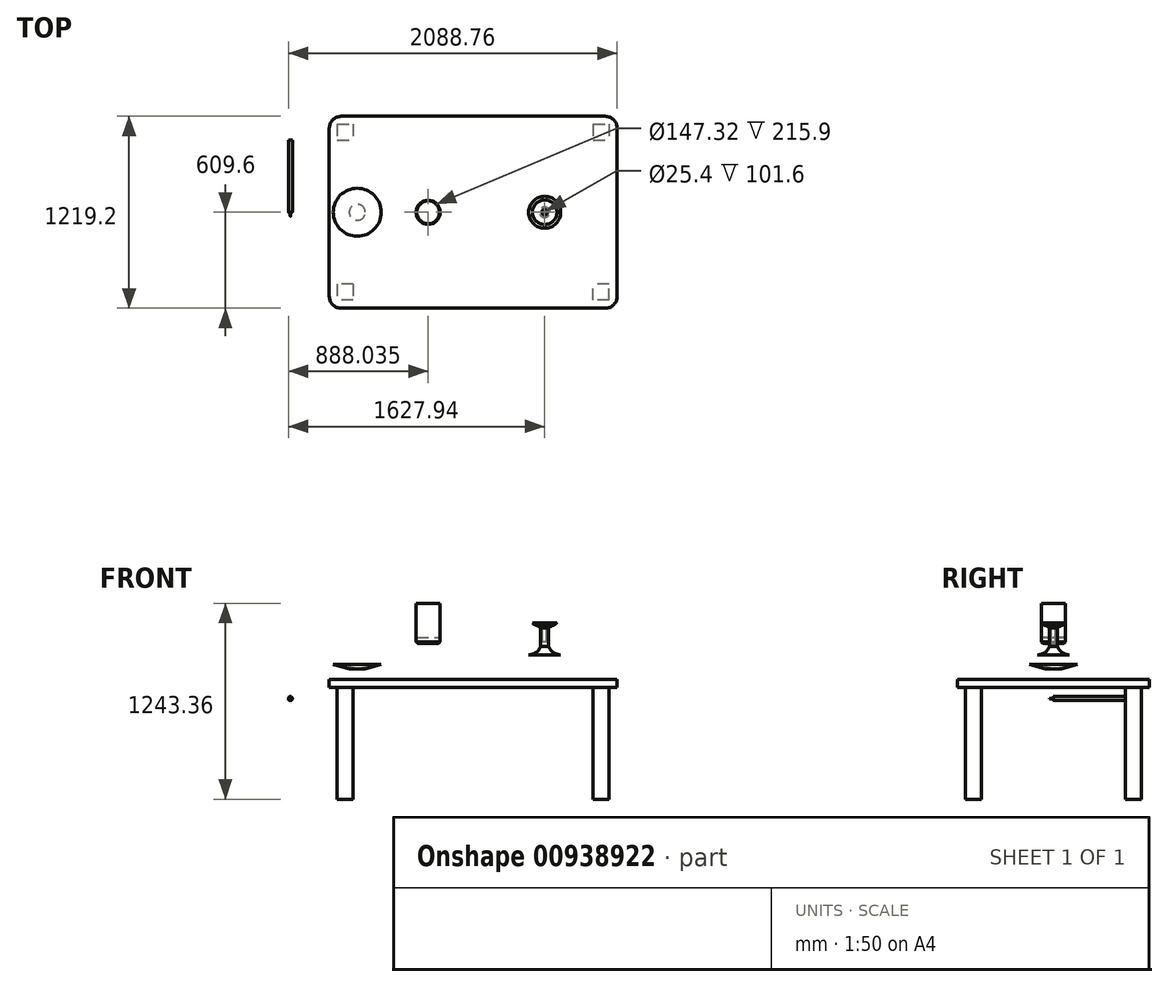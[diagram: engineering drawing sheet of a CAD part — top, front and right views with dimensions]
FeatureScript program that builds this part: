
annotation { "Feature Type Name" : "Feature", "Feature Type Description" : "" }
export const myFeature = defineFeature(function(context is Context, id is Id, definition is map)
    precondition{}
    {
        {
            var Q0;
            Q0=qCreatedBy(makeId("Top.planeOp"),FACE);
            var sketch = newSketch(context, id + "F0", { "sketchPlane" : qUnion([Q0])});
            skLineSegment(sketch, "E0.bottom", {"start": v(-838.2, 609.6) * mm, "end": v(838.2, 609.6) * mm});
            skLineSegment(sketch, "E0.top", {"start": v(-838.2, -609.6) * mm, "end": v(838.2, -609.6) * mm});
            skLineSegment(sketch, "E0.left", {"start": v(-914.4, 533.4) * mm, "end": v(-914.4, -533.4) * mm});
            skLineSegment(sketch, "E0.right", {"start": v(914.4, 533.4) * mm, "end": v(914.4, -533.4) * mm});
            skPoint(sketch, "E0.middle", {"position": v(0, 0) * mm});
            skLineSegment(sketch, "E1.bottom", {"start": v(-863.6, 558.8) * mm, "end": v(-762, 558.8) * mm});
            skLineSegment(sketch, "E1.top", {"start": v(-863.6, 457.2) * mm, "end": v(-762, 457.2) * mm});
            skLineSegment(sketch, "E1.left", {"start": v(-863.6, 558.8) * mm, "end": v(-863.6, 457.2) * mm});
            skLineSegment(sketch, "E1.right", {"start": v(-762, 558.8) * mm, "end": v(-762, 457.2) * mm});
            skLineSegment(sketch, "E2.bottom", {"start": v(762, 558.8) * mm, "end": v(863.6, 558.8) * mm});
            skLineSegment(sketch, "E2.top", {"start": v(762, 457.2) * mm, "end": v(863.6, 457.2) * mm});
            skLineSegment(sketch, "E2.left", {"start": v(762, 558.8) * mm, "end": v(762, 457.2) * mm});
            skLineSegment(sketch, "E2.right", {"start": v(863.6, 558.8) * mm, "end": v(863.6, 457.2) * mm});
            skLineSegment(sketch, "E3.bottom", {"start": v(863.6, -558.8) * mm, "end": v(762, -558.8) * mm});
            skLineSegment(sketch, "E3.top", {"start": v(863.6, -457.2) * mm, "end": v(762, -457.2) * mm});
            skLineSegment(sketch, "E3.left", {"start": v(863.6, -558.8) * mm, "end": v(863.6, -457.2) * mm});
            skLineSegment(sketch, "E3.right", {"start": v(762, -558.8) * mm, "end": v(762, -457.2) * mm});
            skLineSegment(sketch, "E4.bottom", {"start": v(-762, -457.2) * mm, "end": v(-863.6, -457.2) * mm});
            skLineSegment(sketch, "E4.top", {"start": v(-762, -558.8) * mm, "end": v(-863.6, -558.8) * mm});
            skLineSegment(sketch, "E4.left", {"start": v(-762, -457.2) * mm, "end": v(-762, -558.8) * mm});
            skLineSegment(sketch, "E4.right", {"start": v(-863.6, -457.2) * mm, "end": v(-863.6, -558.8) * mm});
            skPoint(sketch, "E5.visualSharp", {"position": v(-914.4, 609.6) * mm});
            skArc(sketch, "E5.filletArc", {"start": v(-838.2, 609.6) * mm, "mid": v(-892.08, 587.28) * mm, "end": v(-914.4, 533.4) * mm});
            skPoint(sketch, "E6.visualSharp", {"position": v(914.4, 609.6) * mm});
            skArc(sketch, "E6.filletArc", {"start": v(914.4, 533.4) * mm, "mid": v(892.08, 587.28) * mm, "end": v(838.2, 609.6) * mm});
            skPoint(sketch, "E7.visualSharp", {"position": v(914.4, -609.6) * mm});
            skArc(sketch, "E7.filletArc", {"start": v(838.2, -609.6) * mm, "mid": v(892.08, -587.28) * mm, "end": v(914.4, -533.4) * mm});
            skPoint(sketch, "E8.visualSharp", {"position": v(-914.4, -609.6) * mm});
            skArc(sketch, "E8.filletArc", {"start": v(-914.4, -533.4) * mm, "mid": v(-892.08, -587.28) * mm, "end": v(-838.2, -609.6) * mm});
            skSolve(sketch);
        }
        {
            var Q0;
            Q0=makeQuery(id+"F0.imprint","IMPRINT",FACE,{"disambiguationData":[TD([[makeQuery(id+"F0.imprint","IMPRINT",EDGE,{"derivedFrom":sQuery(id+"F0.wireOp",EDGE,"E0.bottom")}),-1.0]])]});
            var Q1;
            Q1=makeQuery(id+"F0.imprint","IMPRINT",FACE,{"disambiguationData":[TD([[makeQuery(id+"F0.imprint","IMPRINT",EDGE,{"derivedFrom":sQuery(id+"F0.wireOp",EDGE,"E4.bottom")}),1.0]])]});
            var Q2;
            Q2=makeQuery(id+"F0.imprint","IMPRINT",FACE,{"disambiguationData":[TD([[makeQuery(id+"F0.imprint","IMPRINT",EDGE,{"derivedFrom":sQuery(id+"F0.wireOp",EDGE,"E3.bottom")}),-1.0]])]});
            var Q3;
            Q3=makeQuery(id+"F0.imprint","IMPRINT",FACE,{"disambiguationData":[TD([[makeQuery(id+"F0.imprint","IMPRINT",EDGE,{"derivedFrom":sQuery(id+"F0.wireOp",EDGE,"E2.bottom")}),-1.0]])]});
            var Q4;
            Q4=makeQuery(id+"F0.imprint","IMPRINT",FACE,{"disambiguationData":[TD([[makeQuery(id+"F0.imprint","IMPRINT",EDGE,{"derivedFrom":sQuery(id+"F0.wireOp",EDGE,"E1.bottom")}),-1.0]])]});
            extrude(context, id + "F1", {"entities" : qUnion([Q0, Q1, Q2, Q3, Q4]), "depth" : 50.8 * mm, "offsetDistance" : 25.4 * mm});
        }
        {
            var Q0;
            Q0=makeQuery(id+"F0.imprint","IMPRINT",FACE,{"disambiguationData":[TD([[makeQuery(id+"F0.imprint","IMPRINT",EDGE,{"derivedFrom":sQuery(id+"F0.wireOp",EDGE,"E4.bottom")}),1.0]])]});
            var Q1;
            Q1=makeQuery(id+"F0.imprint","IMPRINT",FACE,{"disambiguationData":[TD([[makeQuery(id+"F0.imprint","IMPRINT",EDGE,{"derivedFrom":sQuery(id+"F0.wireOp",EDGE,"E1.bottom")}),-1.0]])]});
            var Q2;
            Q2=makeQuery(id+"F0.imprint","IMPRINT",FACE,{"disambiguationData":[TD([[makeQuery(id+"F0.imprint","IMPRINT",EDGE,{"derivedFrom":sQuery(id+"F0.wireOp",EDGE,"E2.bottom")}),-1.0]])]});
            var Q3;
            Q3=makeQuery(id+"F0.imprint","IMPRINT",FACE,{"disambiguationData":[TD([[makeQuery(id+"F0.imprint","IMPRINT",EDGE,{"derivedFrom":sQuery(id+"F0.wireOp",EDGE,"E3.bottom")}),-1.0]])]});
            extrude(context, id + "F2", {"entities" : qUnion([Q0, Q1, Q2, Q3]), "operationType" : NewBodyOperationType.ADD, "oppositeDirection" : true, "depth" : 711.2 * mm, "offsetDistance" : 25.4 * mm});
        }
        {
            var Q0;
            Q0=qCreatedBy(makeId("Front.planeOp"),FACE);
            var sketch = newSketch(context, id + "F3", { "sketchPlane" : qUnion([Q0])});
            skLineSegment(sketch, "E9", {"start": v(-286.32, 278.16) * mm, "end": v(-286.32, 532.16) * mm, "construction": true});
            skLineSegment(sketch, "E10.bottom", {"start": v(-286.32, 278.16) * mm, "end": v(-210.12, 278.16) * mm});
            skLineSegment(sketch, "E10.top", {"start": v(-286.32, 316.26) * mm, "end": v(-210.12, 316.26) * mm});
            skLineSegment(sketch, "E10.left", {"start": v(-286.32, 278.16) * mm, "end": v(-286.32, 316.26) * mm});
            skLineSegment(sketch, "E10.right", {"start": v(-210.12, 278.16) * mm, "end": v(-210.12, 316.26) * mm});
            skLineSegment(sketch, "E11.bottom", {"start": v(-210.12, 316.26) * mm, "end": v(-212.66, 316.26) * mm});
            skLineSegment(sketch, "E11.top", {"start": v(-210.12, 532.16) * mm, "end": v(-212.66, 532.16) * mm});
            skLineSegment(sketch, "E11.left", {"start": v(-210.12, 316.26) * mm, "end": v(-210.12, 532.16) * mm});
            skLineSegment(sketch, "E11.right", {"start": v(-212.66, 316.26) * mm, "end": v(-212.66, 532.16) * mm});
            skSolve(sketch);
        }
        {
            var Q0;
            Q0=makeQuery(id+"F3.imprint","IMPRINT",FACE,{"disambiguationData":[TD([[makeQuery(id+"F3.imprint","IMPRINT",EDGE,{"derivedFrom":sQuery(id+"F3.wireOp",EDGE,"E10.bottom")}),1.0]])]});
            var Q1;
            Q1=makeQuery(id+"F3.imprint","IMPRINT",FACE,{"disambiguationData":[TD([[makeQuery(id+"F3.imprint","IMPRINT",EDGE,{"derivedFrom":sQuery(id+"F3.wireOp",EDGE,"E11.top")}),1.0]])]});
            var Q2;
            Q2=sQuery(id+"F3.wireOp",EDGE,"E9");
            revolve(context, id + "F4", {"surfaceOperationType" : NewSurfaceOperationType.NEW, "entities" : qUnion([Q0, Q1]), "axis" : qUnion([Q2]), "revolveType" : RevolveType.FULL});
        }
        {
            var Q0;
            Q0=makeQuery(id+"F4.opRevolve","SWEPT_EDGE",EDGE,{"disambiguationData":[OSD([sQuery(id+"F3.wireOp",EDGE,"E10.bottom"),sQuery(id+"F3.wireOp",EDGE,"E10.right")])]});
            chamfer(context, id + "F5", {"entities" : qUnion([Q0]), "width" : 10.16 * mm, "tangentPropagation" : true});
        }
        {
            var Q0;
            Q0=qCreatedBy(makeId("Front.planeOp"),FACE);
            var sketch = newSketch(context, id + "F6", { "sketchPlane" : qUnion([Q0])});
            skLineSegment(sketch, "E12", {"start": v(-736.83, 117.03) * mm, "end": v(-736.83, 258.84) * mm});
            skLineSegment(sketch, "E13", {"start": v(-736.83, 117.03) * mm, "end": v(-787.63, 117.03) * mm});
            skLineSegment(sketch, "E14", {"start": v(-787.63, 117.03) * mm, "end": v(-889.23, 144.25) * mm});
            skLineSegment(sketch, "E15", {"start": v(-889.23, 144.25) * mm, "end": v(-736.83, 119.57) * mm});
            skSolve(sketch);
        }
        {
            var Q0;
            {var subQ0=sQuery(id+"F6.wireOp",EDGE,"E13");Q0=makeQuery(id+"F6.imprint","IMPRINT",FACE,{"disambiguationData":[TD([[makeQuery(id+"F6.imprint","IMPRINT",EDGE,{"derivedFrom":subQ0}),-1.0]])]});}
            var Q1;
            Q1=sQuery(id+"F6.wireOp",EDGE,"E12");
            revolve(context, id + "F7", {"surfaceOperationType" : NewSurfaceOperationType.NEW, "entities" : qUnion([Q0]), "axis" : qUnion([Q1]), "revolveType" : RevolveType.FULL});
        }
        {
            var Q0;
            Q0=qCreatedBy(makeId("Front.planeOp"),FACE);
            var sketch = newSketch(context, id + "F8", { "sketchPlane" : qUnion([Q0])});
            skCircle(sketch, "E16", {"center": v(-1161.66, -71.9) * mm, "radius": 12.7 * mm});
            skCircle(sketch, "E17", {"center": v(-1161.66, -71.9) * mm, "radius": 1.27 * mm});
            skSolve(sketch);
        }
        {
            var Q0;
            Q0=makeQuery(id+"F8.imprint","IMPRINT",FACE,{"disambiguationData":[TD([[makeQuery(id+"F8.imprint","IMPRINT",EDGE,{"derivedFrom":sQuery(id+"F8.wireOp",EDGE,"E16")}),1.0]])]});
            var Q1;
            Q1=makeQuery(id+"F8.imprint","IMPRINT",FACE,{"disambiguationData":[TD([[makeQuery(id+"F8.imprint","IMPRINT",EDGE,{"derivedFrom":sQuery(id+"F8.wireOp",EDGE,"E17")}),1.0]])]});
            extrude(context, id + "F9", {"entities" : qUnion([Q0, Q1]), "oppositeDirection" : true, "depth" : 457.2 * mm, "offsetDistance" : 25.4 * mm});
        }
        {
            var Q0;
            Q0=makeQuery(id+"F8.imprint","IMPRINT",FACE,{"disambiguationData":[TD([[makeQuery(id+"F8.imprint","IMPRINT",EDGE,{"derivedFrom":sQuery(id+"F8.wireOp",EDGE,"E17")}),1.0]])]});
            extrude(context, id + "F10", {"entities" : qUnion([Q0]), "operationType" : NewBodyOperationType.ADD, "depth" : 25.4 * mm, "offsetDistance" : 25.4 * mm});
        }
        {
            var Q0;
            Q0=makeQuery(id+"F9.opExtrude","CAP_EDGE",EDGE,{"disambiguationData":[OSD([sQuery(id+"F8.wireOp",EDGE,"E16")])],"isStart":true});
            fillet(context, id + "F11", {"entities" : qUnion([Q0]), "radius" : 2.54 * mm, "tangentPropagation" : true, "allowEdgeOverflow" : false});
        }
        {
            var Q0;
            Q0=qCreatedBy(makeId("Front.planeOp"),FACE);
            var sketch = newSketch(context, id + "F12", { "sketchPlane" : qUnion([Q0])});
            skLineSegment(sketch, "E18", {"start": v(453.58, 205.76) * mm, "end": v(453.58, 408.96) * mm});
            skLineSegment(sketch, "E19", {"start": v(453.58, 205.76) * mm, "end": v(351.98, 205.76) * mm});
            skLineSegment(sketch, "E20.bottom", {"start": v(453.58, 260.73) * mm, "end": v(428.18, 260.73) * mm});
            skLineSegment(sketch, "E20.top", {"start": v(453.58, 376.7) * mm, "end": v(428.18, 376.7) * mm});
            skLineSegment(sketch, "E20.left", {"start": v(453.58, 260.73) * mm, "end": v(453.58, 376.7) * mm});
            skLineSegment(sketch, "E20.right", {"start": v(428.18, 260.73) * mm, "end": v(428.18, 376.7) * mm});
            skLineSegment(sketch, "E21.bottom", {"start": v(453.58, 376.7) * mm, "end": v(420.56, 376.7) * mm});
            skLineSegment(sketch, "E21.top", {"start": v(453.58, 389.4) * mm, "end": v(420.56, 389.4) * mm});
            skLineSegment(sketch, "E21.left", {"start": v(453.58, 376.7) * mm, "end": v(453.58, 389.4) * mm});
            skLineSegment(sketch, "E21.right", {"start": v(420.56, 376.7) * mm, "end": v(420.56, 389.4) * mm});
            skLineSegment(sketch, "E22", {"start": v(504.49, 408.96) * mm, "end": v(355.03, 408.96) * mm});
            skArc(sketch, "E23", {"start": v(375.65, 408.96) * mm, "mid": v(396.06, 394.5) * mm, "end": v(420.56, 389.4) * mm});
            skArc(sketch, "E24", {"start": v(351.98, 205.76) * mm, "mid": v(398.96, 220.93) * mm, "end": v(428.18, 260.73) * mm});
            skLineSegment(sketch, "E25", {"start": v(375.65, 408.96) * mm, "end": v(437.07, 389.4) * mm});
            skSolve(sketch);
        }
        {
            var Q0;
            {var subQ3=sQuery(id+"F12.wireOp",EDGE,"E20.top");Q0=makeQuery(id+"F12.imprint","IMPRINT",FACE,{"disambiguationData":[TD([[makeQuery(id+"F12.imprint","IMPRINT",EDGE,{"derivedFrom":subQ3}),-1.0]])]});}
            var Q1;
            {var subQ0=sQuery(id+"F12.wireOp",EDGE,"E20.bottom");Q1=makeQuery(id+"F12.imprint","IMPRINT",FACE,{"disambiguationData":[TD([[makeQuery(id+"F12.imprint","IMPRINT",EDGE,{"derivedFrom":subQ0}),-1.0]])]});}
            var Q2;
            {var subQ2=sQuery(id+"F12.wireOp",EDGE,"E19");Q2=makeQuery(id+"F12.imprint","IMPRINT",FACE,{"disambiguationData":[TD([[makeQuery(id+"F12.imprint","IMPRINT",EDGE,{"derivedFrom":subQ2}),-1.0]])]});}
            var Q3;
            {var subQ2=sQuery(id+"F12.wireOp",EDGE,"E23");Q3=makeQuery(id+"F12.imprint","IMPRINT",FACE,{"disambiguationData":[TD([[makeQuery(id+"F12.imprint","IMPRINT",EDGE,{"derivedFrom":subQ2}),1.0]])]});}
            var Q4;
            Q4=sQuery(id+"F12.wireOp",EDGE,"E18");
            revolve(context, id + "F13", {"surfaceOperationType" : NewSurfaceOperationType.NEW, "entities" : qUnion([Q0, Q1, Q2, Q3]), "axis" : qUnion([Q4]), "revolveType" : RevolveType.FULL});
        }
        {
            var Q0;
            Q0=makeQuery(id+"F13.opRevolve","SWEPT_FACE",FACE,{"disambiguationData":[OSD([sQuery(id+"F12.wireOp",EDGE,"E21.top")])]});
            var sketch = newSketch(context, id + "F14", { "sketchPlane" : qUnion([Q0])});
            skCircle(sketch, "E26", {"center": v(453.58, 0) * mm, "radius": 12.7 * mm});
            skSolve(sketch);
        }
        {
            var Q0;
            Q0=makeQuery(id+"F14.imprint","IMPRINT",FACE,{"disambiguationData":[TD([[makeQuery(id+"F14.imprint","IMPRINT",EDGE,{"derivedFrom":sQuery(id+"F14.wireOp",EDGE,"E26")}),1.0]])]});
            extrude(context, id + "F15", {"entities" : qUnion([Q0]), "operationType" : NewBodyOperationType.REMOVE, "oppositeDirection" : true, "depth" : 101.6 * mm, "offsetDistance" : 25.4 * mm});
        }
    });
